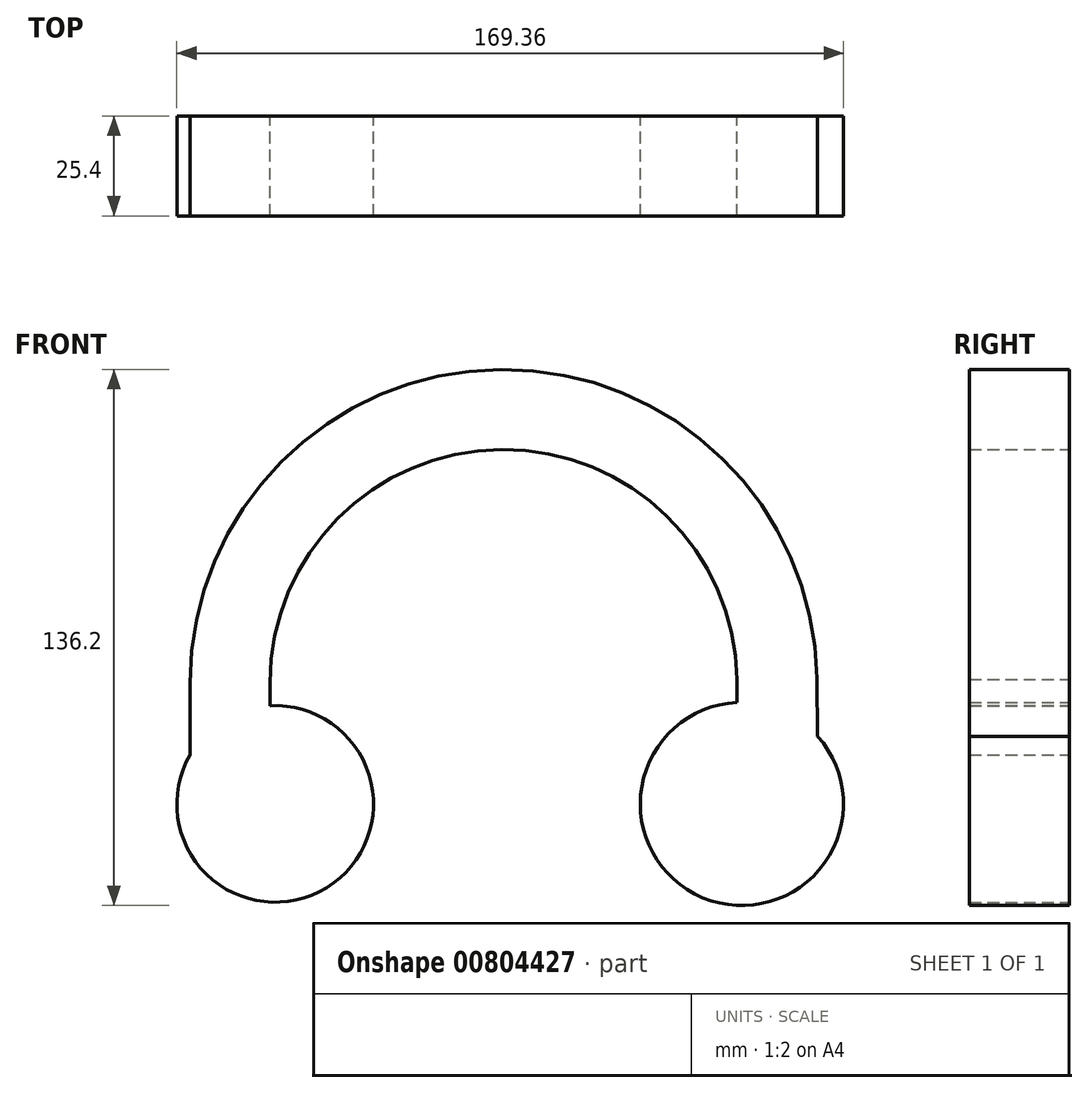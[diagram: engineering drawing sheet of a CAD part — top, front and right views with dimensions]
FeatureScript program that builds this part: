
annotation { "Feature Type Name" : "Feature", "Feature Type Description" : "" }
export const myFeature = defineFeature(function(context is Context, id is Id, definition is map)
    precondition{}
    {
        {
            var Q0;
            Q0=qCreatedBy(makeId("Front.planeOp"),FACE);
            var sketch = newSketch(context, id + "F0", { "sketchPlane" : qUnion([Q0])});
            skCircle(sketch, "E0", {"center": v(-67.46, 10.71) * mm, "radius": 24.98 * mm});
            skCircle(sketch, "E1", {"center": v(51.11, 10.71) * mm, "radius": 25.8 * mm});
            skLineSegment(sketch, "E2", {"start": v(-68.76, 35.66) * mm, "end": v(-68.76, 41.48) * mm});
            skLineSegment(sketch, "E3", {"start": v(49.84, 36.5) * mm, "end": v(49.84, 42.35) * mm});
            skArc(sketch, "E4", {"start": v(-68.76, 41.48) * mm, "mid": v(-9.9, 100.78) * mm, "end": v(49.84, 42.35) * mm});
            skArc(sketch, "E5.0", {"start": v(-89.08, 41.48) * mm, "mid": v(-10.05, 121.1) * mm, "end": v(70.15, 42.65) * mm});
            skLineSegment(sketch, "E6", {"start": v(-89.08, 41.48) * mm, "end": v(-89.08, 23.22) * mm});
            skLineSegment(sketch, "E7", {"start": v(70.15, 42.65) * mm, "end": v(70.37, 27.9) * mm});
            skSolve(sketch);
        }
        {
            var Q0;
            Q0 = qSketchRegion(id + "F0", true);
            extrude(context, id + "F1", {"entities" : qUnion([Q0]), "depth" : 25.4 * mm, "offsetDistance" : 25.4 * mm});
        }
    });
